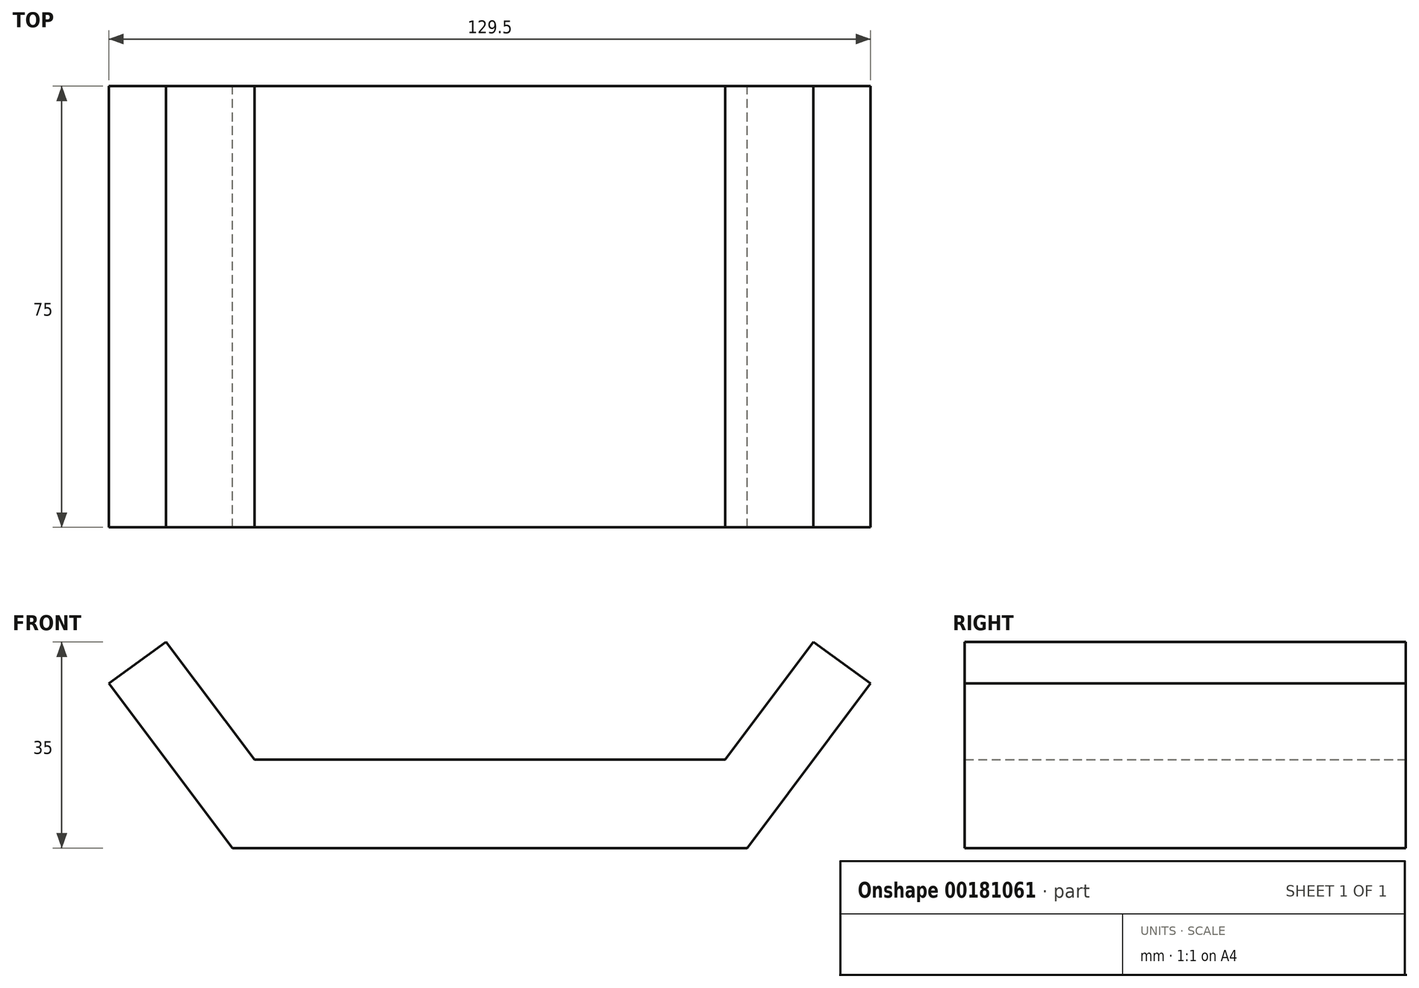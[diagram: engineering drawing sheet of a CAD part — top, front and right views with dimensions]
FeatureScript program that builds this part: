
annotation { "Feature Type Name" : "Feature", "Feature Type Description" : "" }
export const myFeature = defineFeature(function(context is Context, id is Id, definition is map)
    precondition{}
    {
        {
            var Q0;
            Q0=qCreatedBy(makeId("Front.planeOp"),FACE);
            var sketch = newSketch(context, id + "F0", { "sketchPlane" : qUnion([Q0])});
            skLineSegment(sketch, "E0", {"start": v(-43.75, 0) * mm, "end": v(43.75, 0) * mm});
            skLineSegment(sketch, "E1", {"start": v(43.75, 0) * mm, "end": v(64.75, 28) * mm});
            skLineSegment(sketch, "E2", {"start": v(64.75, 28) * mm, "end": v(55, 35) * mm});
            skLineSegment(sketch, "E3", {"start": v(55, 35) * mm, "end": v(40, 15) * mm});
            skLineSegment(sketch, "E4", {"start": v(40, 15) * mm, "end": v(-40, 15) * mm});
            skLineSegment(sketch, "E5", {"start": v(-40, 15) * mm, "end": v(-55, 35) * mm});
            skLineSegment(sketch, "E6", {"start": v(-55, 35) * mm, "end": v(-64.75, 28) * mm});
            skLineSegment(sketch, "E7", {"start": v(-64.75, 28) * mm, "end": v(-43.75, 0) * mm});
            skSolve(sketch);
        }
        {
            var Q0;
            Q0 = qSketchRegion(id + "F0", true);
            extrude(context, id + "F1", {"entities" : qUnion([Q0]), "depth" : 75 * mm});
        }
    });
